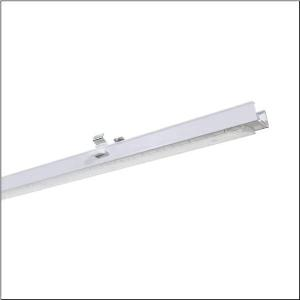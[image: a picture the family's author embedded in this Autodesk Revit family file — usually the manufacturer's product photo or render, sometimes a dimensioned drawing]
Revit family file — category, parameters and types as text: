
# Revit family: trunking_flex_31_51re18mb48b
name_source: partatom
category: Lighting Fixtures
units: mm (PartAtom-declared; Revit-internal decimal feet)

## family parameters
Cut with Voids When Loaded = No
Host = Face
Light Source = No
Part Type = Normal
Room Calculation Point = No
Round Connector Dimension = Use Diameter
Shared = No

## types (1)
- --- (1 x LED, 8000 lm, 50 W, 4000K)
    Apparent Load = 50 VA
    CIE Flux Codes = 71 89 97 97 100
    Color Rendering = 80
    Color Temperature = 4000K
    Default Elevation = 1800 mm
    Description = Trunking Flex 31, luminaire insert, of extruded aluminium section, coated, traffic white (RAL 9016), length: 1.472mm, width: 91mm, height: 53mm, LED rated luminous flux: 8.000lm, light colour: 840, control gear: ON/OFF Multilumen, with system connector: socket, mains connection: 220..240V, AC, 50/60Hz, rated input power: 50W, luminous flux adjustable on luminaire in four steps (4130/5610/6850/8000lm), connected load according to luminous flux setting (25/34/42/50W), primary light control with lens, of plastic, primary optical cover: cover, of PMMA, light emission: direct distribution, protection rating (complete): IP20, insulation class (complete): insulation class I (protective earthing), certification: CE, UKCA, impact resistance: IK02, permissible ambient temperature for indoor applications: -20..+40°C, packaging unit: 1 piece
    Height = 58 mm
    Lamp = 1 x LED
    Lamp Light Flux = 8000 lm
    Lamp Power = 50 W
    Lamp count = 1
    Length = 1472 mm
    Luminous efficacy = 160 lm/W
    Manufacturer = Siteco
    ModVariant = No
    Model = 51RE18MB48B
    Mounting Place = Ceiling
    Mounting Type = Pendant
    Number of Poles = 1
    OnlyDefault = Yes
    Power Factor = 1
    Product Name = Trunking Flex 31
    Product group = luminaire insert
    ProductGroupID = 901
    Protection Class = Protection class I
    Protection Degree = IP 20
    RLX_Detail_Level = 1
    RLX_Emergency_Light_Flux = 0 lm
    RLX_Emergency_Type = 0
    RLX_Emergency_Type_DB = No
    RlxData = <blob elided: 20405 chars, md5=8040a499>
    Socket = socket
    Standby Power = 0 W
    System Light Flux = 8000 lm
    System Power = 50 W
    Type Comments = factory setting: luminous flux: 100 % | (ON | ON) | 300 mA
    Type Image = l_1266702.jpg
    URL = http://relux.com
    VarID = @adj_018577
    Voltage = 0 V
    Weight = 0.00 kg
    Width = 65 mm

## geometry (parser evidence)
native form markers: Blend x4, Sweep x11
no freeform markers — native parametric forms only
